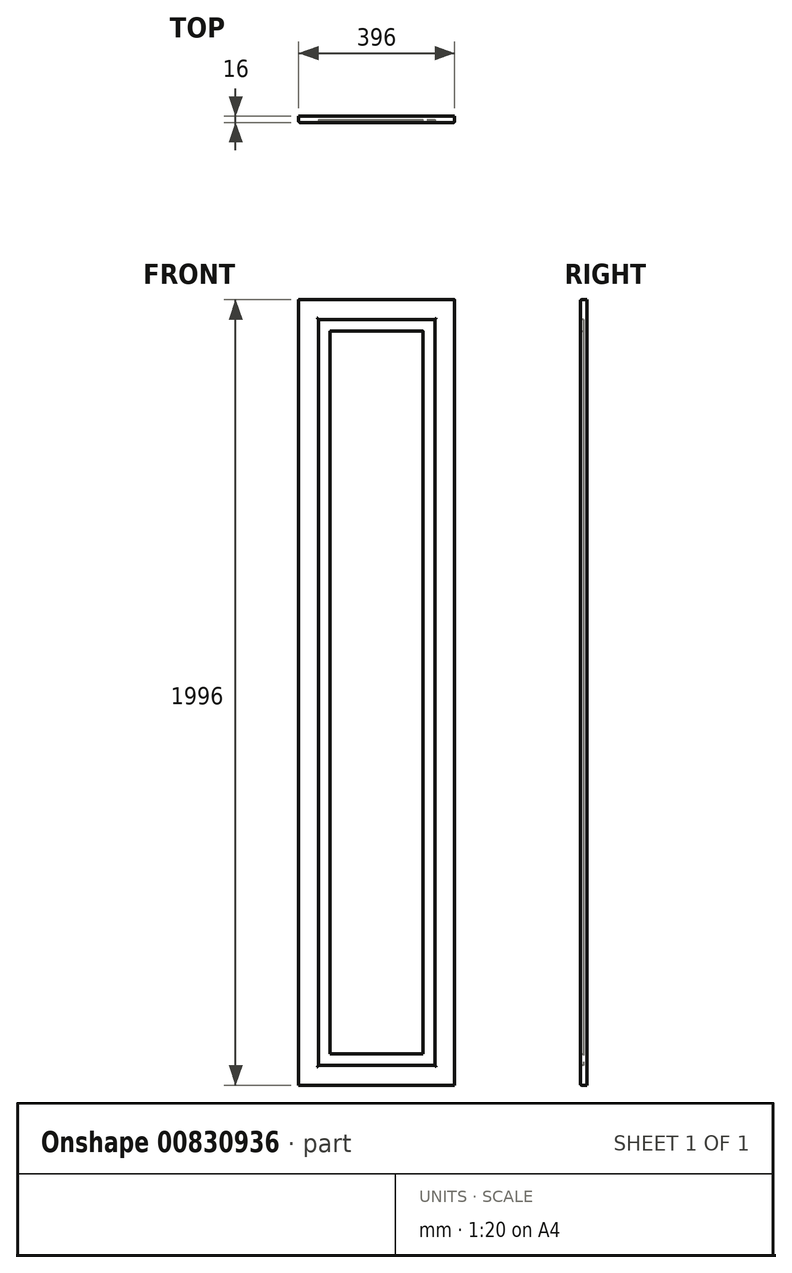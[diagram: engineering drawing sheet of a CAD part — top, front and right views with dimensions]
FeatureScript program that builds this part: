
annotation { "Feature Type Name" : "Feature", "Feature Type Description" : "" }
export const myFeature = defineFeature(function(context is Context, id is Id, definition is map)
    precondition{}
    {
        {
            var Q0;
            Q0=qCreatedBy(makeId("Front.planeOp"),FACE);
            var sketch = newSketch(context, id + "F0", { "sketchPlane" : qUnion([Q0])});
            skLineSegment(sketch, "E0.bottom", {"start": v(0, 0) * mm, "end": v(44.66, 0) * mm});
            skLineSegment(sketch, "E0.top", {"start": v(0, 33.8) * mm, "end": v(44.66, 33.8) * mm});
            skLineSegment(sketch, "E0.left", {"start": v(0, 0) * mm, "end": v(0, 33.8) * mm});
            skLineSegment(sketch, "E0.right", {"start": v(44.66, 0) * mm, "end": v(44.66, 33.8) * mm});
            skSolve(sketch);
        }
        {
            var Q0;
            Q0=makeQuery(id+"F0.imprint","IMPRINT",FACE,{"disambiguationData":[TD([[makeQuery(id+"F0.imprint","IMPRINT",EDGE,{"derivedFrom":sQuery(id+"F0.wireOp",EDGE,"E0.bottom")}),1.0]])]});
            extrude(context, id + "F1", {"entities" : qUnion([Q0]), "depth" : 16 * mm, "offsetDistance" : 25.4 * mm});
        }
        {
            var Q0;
            Q0=makeQuery(id+"F1.opExtrude","SWEPT_FACE",FACE,{"disambiguationData":[OSD([sQuery(id+"F0.wireOp",EDGE,"E0.bottom")])]});
            extrude(context, id + "F2", {"entities" : qUnion([Q0]), "operationType" : NewBodyOperationType.ADD, "oppositeDirection" : true, "depth" : 796 * mm, "offsetDistance" : 25 * mm});
        }
        {
            var Q0;
            {var subQ0=sQuery(id+"F0.wireOp",EDGE,"E0.left");Q0=makeQuery(id+"F2.boolean.opBoolean","MERGE",FACE,{"derivedFrom":[makeQuery(id+"F1.opExtrude","SWEPT_FACE",FACE,{"disambiguationData":[OSD([subQ0])]}),makeQuery(id+"F2.opExtrude","SWEPT_FACE",FACE,{"disambiguationData":[OSD([sQuery(id+"F0.wireOp",EDGE,"E0.bottom"),subQ0])]})]});}
            extrude(context, id + "F3", {"entities" : qUnion([Q0]), "operationType" : NewBodyOperationType.ADD, "oppositeDirection" : true, "depth" : 196 * mm, "offsetDistance" : 25 * mm});
        }
        {
            var Q0;
            {var subQ0=sQuery(id+"F0.wireOp",EDGE,"E0.left");var subQ1=sQuery(id+"F0.wireOp",EDGE,"E0.bottom");Q0=makeQuery(id+"F3.boolean.opBoolean","MERGE",FACE,{"derivedFrom":[makeQuery(id+"F2.boolean.opBoolean","MERGE",FACE,{"derivedFrom":[makeQuery(id+"F1.opExtrude","CAP_FACE",FACE,{"disambiguationData":[OSD([subQ1,sQuery(id+"F0.wireOp",EDGE,"E0.top"),subQ0,sQuery(id+"F0.wireOp",EDGE,"E0.right")])],"isStart":false}),makeQuery(id+"F2.opExtrude","SWEPT_FACE",FACE,{"disambiguationData":[OSD([subQ1]),TDD([makeQuery(id+"F1.opExtrude","CAP_EDGE",EDGE,{"disambiguationData":[OSD([subQ1])],"isStart":false})])]})]}),makeQuery(id+"F3.opExtrude","SWEPT_FACE",FACE,{"disambiguationData":[OSD([subQ1,subQ0]),TDD([makeQuery(id+"F2.boolean.opBoolean","MERGE",EDGE,{"derivedFrom":[makeQuery(id+"F1.opExtrude","CAP_EDGE",EDGE,{"disambiguationData":[OSD([subQ0])],"isStart":false}),makeQuery(id+"F2.opExtrude","SWEPT_EDGE",EDGE,{"disambiguationData":[OSD([subQ1,subQ0]),TDD([makeQuery(id+"F1.opExtrude","CAP_VERTEX",VERTEX,{"disambiguationData":[OSD([subQ1,subQ0])],"isStart":false})])]})]})])]})]});}
            var sketch = newSketch(context, id + "F4", { "sketchPlane" : qUnion([Q0])});
            skLineSegment(sketch, "E1.bottom", {"start": v(59.7, 646.67) * mm, "end": v(128.66, 646.67) * mm});
            skLineSegment(sketch, "E1.top", {"start": v(59.7, 152.97) * mm, "end": v(128.66, 152.97) * mm});
            skLineSegment(sketch, "E1.left", {"start": v(59.7, 646.67) * mm, "end": v(59.7, 152.97) * mm});
            skLineSegment(sketch, "E1.right", {"start": v(128.66, 646.67) * mm, "end": v(128.66, 152.97) * mm});
            skSolve(sketch);
        }
        {
            var Q0;
            Q0=makeQuery(id+"F4.imprint","IMPRINT",FACE,{"disambiguationData":[TD([[makeQuery(id+"F4.imprint","IMPRINT",EDGE,{"derivedFrom":sQuery(id+"F4.wireOp",EDGE,"E1.bottom")}),-1.0]])]});
            extrude(context, id + "F5", {"entities" : qUnion([Q0]), "operationType" : NewBodyOperationType.REMOVE, "oppositeDirection" : true, "depth" : 7 * mm, "offsetDistance" : 25 * mm});
        }
        {
            var Q0;
            Q0=makeQuery(id+"F5.boolean.opBoolean","COPY",FACE,{"derivedFrom":makeQuery(id+"F5.opExtrude","SWEPT_FACE",FACE,{"disambiguationData":[OSD([sQuery(id+"F4.wireOp",EDGE,"E1.left")])]})});
            extrude(context, id + "F6", {"entities" : qUnion([Q0]), "operationType" : NewBodyOperationType.REMOVE, "oppositeDirection" : true, "depth" : 9.7 * mm, "offsetDistance" : 25 * mm});
        }
        {
            var Q0;
            {var subQ0=sQuery(id+"F4.wireOp",EDGE,"E1.bottom");Q0=makeQuery(id+"F6.boolean.opBoolean","MERGE",FACE,{"derivedFrom":[makeQuery(id+"F5.boolean.opBoolean","COPY",FACE,{"derivedFrom":makeQuery(id+"F5.opExtrude","SWEPT_FACE",FACE,{"disambiguationData":[OSD([subQ0])]})}),makeQuery(id+"F6.opExtrude","SWEPT_FACE",FACE,{"disambiguationData":[OSD([subQ0,sQuery(id+"F4.wireOp",EDGE,"E1.left")])]})]});}
            extrude(context, id + "F7", {"entities" : qUnion([Q0]), "operationType" : NewBodyOperationType.ADD, "oppositeDirection" : true, "depth" : 99.33 * mm, "offsetDistance" : 25 * mm});
        }
        {
            var Q0;
            {var subQ0=sQuery(id+"F4.wireOp",EDGE,"E1.bottom");Q0=makeQuery(id+"F6.boolean.opBoolean","MERGE",FACE,{"derivedFrom":[makeQuery(id+"F5.boolean.opBoolean","COPY",FACE,{"derivedFrom":makeQuery(id+"F5.opExtrude","SWEPT_FACE",FACE,{"disambiguationData":[OSD([subQ0])]})}),makeQuery(id+"F6.opExtrude","SWEPT_FACE",FACE,{"disambiguationData":[OSD([subQ0,sQuery(id+"F4.wireOp",EDGE,"E1.left")])]})]});}
            extrude(context, id + "F8", {"entities" : qUnion([Q0]), "operationType" : NewBodyOperationType.REMOVE, "oppositeDirection" : true, "depth" : 99.33 * mm, "offsetDistance" : 25 * mm});
        }
        {
            var Q0;
            {var subQ0=sQuery(id+"F4.wireOp",EDGE,"E1.right");Q0=makeQuery(id+"F8.boolean.opBoolean","MERGE",FACE,{"derivedFrom":[makeQuery(id+"F5.boolean.opBoolean","COPY",FACE,{"derivedFrom":makeQuery(id+"F5.opExtrude","SWEPT_FACE",FACE,{"disambiguationData":[OSD([subQ0])]})}),makeQuery(id+"F8.opExtrude","SWEPT_FACE",FACE,{"disambiguationData":[OSD([sQuery(id+"F4.wireOp",EDGE,"E1.bottom"),subQ0])]})]});}
            extrude(context, id + "F9", {"entities" : qUnion([Q0]), "operationType" : NewBodyOperationType.REMOVE, "oppositeDirection" : true, "depth" : 17.34 * mm, "offsetDistance" : 25 * mm});
        }
        {
            var Q0;
            {var subQ0=sQuery(id+"F4.wireOp",EDGE,"E1.top");Q0=makeQuery(id+"F9.boolean.opBoolean","MERGE",FACE,{"derivedFrom":[makeQuery(id+"F6.boolean.opBoolean","MERGE",FACE,{"derivedFrom":[makeQuery(id+"F5.boolean.opBoolean","COPY",FACE,{"derivedFrom":makeQuery(id+"F5.opExtrude","SWEPT_FACE",FACE,{"disambiguationData":[OSD([subQ0])]})}),makeQuery(id+"F6.opExtrude","SWEPT_FACE",FACE,{"disambiguationData":[OSD([subQ0,sQuery(id+"F4.wireOp",EDGE,"E1.left")])]})]}),makeQuery(id+"F9.opExtrude","SWEPT_FACE",FACE,{"disambiguationData":[OSD([subQ0,sQuery(id+"F4.wireOp",EDGE,"E1.right")])]})]});}
            extrude(context, id + "F10", {"entities" : qUnion([Q0]), "operationType" : NewBodyOperationType.REMOVE, "oppositeDirection" : true, "depth" : 102.97 * mm, "offsetDistance" : 25 * mm});
        }
        {
            var Q0;
            {var subQ0=sQuery(id+"F4.wireOp",EDGE,"E1.right");var subQ1=sQuery(id+"F4.wireOp",EDGE,"E1.top");var subQ2=sQuery(id+"F4.wireOp",EDGE,"E1.left");var subQ3=sQuery(id+"F4.wireOp",EDGE,"E1.bottom");Q0=makeQuery(id+"F10.boolean.opBoolean","MERGE",FACE,{"derivedFrom":[makeQuery(id+"F9.boolean.opBoolean","MERGE",FACE,{"derivedFrom":[makeQuery(id+"F8.boolean.opBoolean","MERGE",FACE,{"derivedFrom":[makeQuery(id+"F6.boolean.opBoolean","MERGE",FACE,{"derivedFrom":[makeQuery(id+"F5.boolean.opBoolean","COPY",FACE,{"derivedFrom":makeQuery(id+"F5.opExtrude","CAP_FACE",FACE,{"disambiguationData":[OSD([subQ3,subQ1,subQ2,subQ0])],"isStart":false})}),makeQuery(id+"F6.opExtrude","SWEPT_FACE",FACE,{"disambiguationData":[OSD([subQ2]),TDD([makeQuery(id+"F5.boolean.opBoolean","COPY",EDGE,{"derivedFrom":makeQuery(id+"F5.opExtrude","CAP_EDGE",EDGE,{"disambiguationData":[OSD([subQ2])],"isStart":false})})])]})]}),makeQuery(id+"F8.opExtrude","SWEPT_FACE",FACE,{"disambiguationData":[OSD([subQ3,subQ2]),TDD([makeQuery(id+"F6.boolean.opBoolean","MERGE",EDGE,{"derivedFrom":[makeQuery(id+"F5.boolean.opBoolean","COPY",EDGE,{"derivedFrom":makeQuery(id+"F5.opExtrude","CAP_EDGE",EDGE,{"disambiguationData":[OSD([subQ3])],"isStart":false})}),makeQuery(id+"F6.opExtrude","SWEPT_EDGE",EDGE,{"disambiguationData":[OSD([subQ3,subQ2]),TDD([makeQuery(id+"F5.boolean.opBoolean","COPY",VERTEX,{"derivedFrom":makeQuery(id+"F5.opExtrude","CAP_VERTEX",VERTEX,{"disambiguationData":[OSD([subQ3,subQ2])],"isStart":false})})])]})]})])]})]}),makeQuery(id+"F9.opExtrude","SWEPT_FACE",FACE,{"disambiguationData":[OSD([subQ3,subQ0]),TDD([makeQuery(id+"F8.boolean.opBoolean","MERGE",EDGE,{"derivedFrom":[makeQuery(id+"F5.boolean.opBoolean","COPY",EDGE,{"derivedFrom":makeQuery(id+"F5.opExtrude","CAP_EDGE",EDGE,{"disambiguationData":[OSD([subQ0])],"isStart":false})}),makeQuery(id+"F8.opExtrude","SWEPT_EDGE",EDGE,{"disambiguationData":[OSD([subQ3,subQ0]),TDD([makeQuery(id+"F5.boolean.opBoolean","COPY",VERTEX,{"derivedFrom":makeQuery(id+"F5.opExtrude","CAP_VERTEX",VERTEX,{"disambiguationData":[OSD([subQ3,subQ0])],"isStart":false})})])]})]})])]})]}),makeQuery(id+"F10.opExtrude","SWEPT_FACE",FACE,{"disambiguationData":[OSD([subQ1,subQ2,subQ0]),TDD([makeQuery(id+"F9.boolean.opBoolean","MERGE",EDGE,{"derivedFrom":[makeQuery(id+"F6.boolean.opBoolean","MERGE",EDGE,{"derivedFrom":[makeQuery(id+"F5.boolean.opBoolean","COPY",EDGE,{"derivedFrom":makeQuery(id+"F5.opExtrude","CAP_EDGE",EDGE,{"disambiguationData":[OSD([subQ1])],"isStart":false})}),makeQuery(id+"F6.opExtrude","SWEPT_EDGE",EDGE,{"disambiguationData":[OSD([subQ1,subQ2]),TDD([makeQuery(id+"F5.boolean.opBoolean","COPY",VERTEX,{"derivedFrom":makeQuery(id+"F5.opExtrude","CAP_VERTEX",VERTEX,{"disambiguationData":[OSD([subQ1,subQ2])],"isStart":false})})])]})]}),makeQuery(id+"F9.opExtrude","SWEPT_EDGE",EDGE,{"disambiguationData":[OSD([subQ1,subQ0]),TDD([makeQuery(id+"F5.boolean.opBoolean","COPY",VERTEX,{"derivedFrom":makeQuery(id+"F5.opExtrude","CAP_VERTEX",VERTEX,{"disambiguationData":[OSD([subQ1,subQ0])],"isStart":false})})])]})]})])]})]});}
            var sketch = newSketch(context, id + "F11", { "sketchPlane" : qUnion([Q0])});
            skLineSegment(sketch, "E2.bottom", {"start": v(74.13, 678.73) * mm, "end": v(109.41, 678.73) * mm});
            skLineSegment(sketch, "E2.top", {"start": v(74.13, 186.63) * mm, "end": v(109.41, 186.63) * mm});
            skLineSegment(sketch, "E2.left", {"start": v(74.13, 678.73) * mm, "end": v(74.13, 186.63) * mm});
            skLineSegment(sketch, "E2.right", {"start": v(109.41, 678.73) * mm, "end": v(109.41, 186.63) * mm});
            skSolve(sketch);
        }
        {
            var Q0;
            Q0=makeQuery(id+"F11.imprint","IMPRINT",FACE,{"disambiguationData":[TD([[makeQuery(id+"F11.imprint","IMPRINT",EDGE,{"derivedFrom":sQuery(id+"F11.wireOp",EDGE,"E2.bottom")}),-1.0]])]});
            extrude(context, id + "F12", {"entities" : qUnion([Q0]), "operationType" : NewBodyOperationType.ADD, "depth" : 7 * mm, "offsetDistance" : 25 * mm});
        }
        {
            var Q0;
            Q0=makeQuery(id+"F12.opExtrude","SWEPT_FACE",FACE,{"disambiguationData":[OSD([sQuery(id+"F11.wireOp",EDGE,"E2.bottom")])]});
            extrude(context, id + "F13", {"entities" : qUnion([Q0]), "operationType" : NewBodyOperationType.ADD, "depth" : 37.27 * mm, "offsetDistance" : 25 * mm});
        }
        {
            var Q0;
            {var subQ0=sQuery(id+"F11.wireOp",EDGE,"E2.right");Q0=makeQuery(id+"F13.boolean.opBoolean","MERGE",FACE,{"derivedFrom":[makeQuery(id+"F12.opExtrude","SWEPT_FACE",FACE,{"disambiguationData":[OSD([subQ0])]}),makeQuery(id+"F13.opExtrude","SWEPT_FACE",FACE,{"disambiguationData":[OSD([sQuery(id+"F11.wireOp",EDGE,"E2.bottom"),subQ0])]})]});}
            extrude(context, id + "F14", {"entities" : qUnion([Q0]), "operationType" : NewBodyOperationType.ADD, "depth" : 6.58 * mm, "offsetDistance" : 25 * mm});
        }
        {
            var Q0;
            {var subQ0=sQuery(id+"F11.wireOp",EDGE,"E2.top");Q0=makeQuery(id+"F14.boolean.opBoolean","MERGE",FACE,{"derivedFrom":[makeQuery(id+"F12.opExtrude","SWEPT_FACE",FACE,{"disambiguationData":[OSD([subQ0])]}),makeQuery(id+"F14.opExtrude","SWEPT_FACE",FACE,{"disambiguationData":[OSD([subQ0,sQuery(id+"F11.wireOp",EDGE,"E2.right")])]})]});}
            extrude(context, id + "F15", {"entities" : qUnion([Q0]), "operationType" : NewBodyOperationType.ADD, "depth" : 106.63 * mm, "offsetDistance" : 25 * mm});
        }
        {
            var Q0;
            {var subQ0=sQuery(id+"F11.wireOp",EDGE,"E2.left");Q0=makeQuery(id+"F15.boolean.opBoolean","MERGE",FACE,{"derivedFrom":[makeQuery(id+"F13.boolean.opBoolean","MERGE",FACE,{"derivedFrom":[makeQuery(id+"F12.opExtrude","SWEPT_FACE",FACE,{"disambiguationData":[OSD([subQ0])]}),makeQuery(id+"F13.opExtrude","SWEPT_FACE",FACE,{"disambiguationData":[OSD([sQuery(id+"F11.wireOp",EDGE,"E2.bottom"),subQ0])]})]}),makeQuery(id+"F15.opExtrude","SWEPT_FACE",FACE,{"disambiguationData":[OSD([sQuery(id+"F11.wireOp",EDGE,"E2.top"),subQ0])]})]});}
            extrude(context, id + "F16", {"entities" : qUnion([Q0]), "operationType" : NewBodyOperationType.REMOVE, "oppositeDirection" : true, "depth" : 5.87 * mm, "offsetDistance" : 25 * mm});
        }
        {
            var Q0;
            Q0=makeQuery(id+"F3.opExtrude","CAP_FACE",FACE,{"disambiguationData":[OSD([sQuery(id+"F0.wireOp",EDGE,"E0.bottom"),sQuery(id+"F0.wireOp",EDGE,"E0.left")])],"isStart":false});
            extrude(context, id + "F17", {"entities" : qUnion([Q0]), "operationType" : NewBodyOperationType.ADD, "depth" : 200 * mm, "offsetDistance" : 25 * mm});
        }
        {
            var Q0;
            {var subQ0=sQuery(id+"F4.wireOp",EDGE,"E1.right");Q0=makeQuery(id+"F10.boolean.opBoolean","MERGE",FACE,{"derivedFrom":[makeQuery(id+"F9.boolean.opBoolean","COPY",FACE,{"derivedFrom":makeQuery(id+"F9.opExtrude","CAP_FACE",FACE,{"disambiguationData":[OSD([sQuery(id+"F4.wireOp",EDGE,"E1.bottom"),subQ0])],"isStart":false})}),makeQuery(id+"F10.opExtrude","SWEPT_FACE",FACE,{"disambiguationData":[OSD([sQuery(id+"F4.wireOp",EDGE,"E1.top"),subQ0])]})]});}
            extrude(context, id + "F18", {"entities" : qUnion([Q0]), "operationType" : NewBodyOperationType.REMOVE, "oppositeDirection" : true, "depth" : 200 * mm, "offsetDistance" : 25 * mm});
        }
        {
            var Q0;
            {var subQ0=sQuery(id+"F11.wireOp",EDGE,"E2.right");var subQ1=sQuery(id+"F11.wireOp",EDGE,"E2.top");Q0=makeQuery(id+"F15.boolean.opBoolean","MERGE",FACE,{"derivedFrom":[makeQuery(id+"F14.opExtrude","CAP_FACE",FACE,{"disambiguationData":[OSD([sQuery(id+"F11.wireOp",EDGE,"E2.bottom"),subQ0])],"isStart":false}),makeQuery(id+"F15.opExtrude","SWEPT_FACE",FACE,{"disambiguationData":[OSD([subQ1,subQ0]),TDD([makeQuery(id+"F14.opExtrude","CAP_EDGE",EDGE,{"disambiguationData":[OSD([subQ1,subQ0])],"isStart":false})])]})]});}
            extrude(context, id + "F19", {"entities" : qUnion([Q0]), "operationType" : NewBodyOperationType.ADD, "depth" : 200 * mm, "offsetDistance" : 25 * mm});
        }
        {
            var Q0;
            Q0=makeQuery(id+"F17.opExtrude","CAP_FACE",FACE,{"disambiguationData":[OSD([sQuery(id+"F0.wireOp",EDGE,"E0.bottom"),sQuery(id+"F0.wireOp",EDGE,"E0.left")])],"isStart":false});
            extrude(context, id + "F20", {"entities" : qUnion([Q0]), "operationType" : NewBodyOperationType.ADD, "depth" : 200 * mm, "offsetDistance" : 25 * mm});
        }
        {
            var Q0;
            Q0=makeQuery(id+"F18.boolean.opBoolean","COPY",FACE,{"derivedFrom":makeQuery(id+"F18.opExtrude","CAP_FACE",FACE,{"disambiguationData":[OSD([sQuery(id+"F4.wireOp",EDGE,"E1.bottom"),sQuery(id+"F4.wireOp",EDGE,"E1.top"),sQuery(id+"F4.wireOp",EDGE,"E1.right")])],"isStart":false})});
            extrude(context, id + "F21", {"entities" : qUnion([Q0]), "operationType" : NewBodyOperationType.REMOVE, "oppositeDirection" : true, "depth" : 200 * mm, "offsetDistance" : 25 * mm});
        }
        {
            var Q0;
            Q0=makeQuery(id+"F19.opExtrude","CAP_FACE",FACE,{"disambiguationData":[OSD([sQuery(id+"F11.wireOp",EDGE,"E2.bottom"),sQuery(id+"F11.wireOp",EDGE,"E2.top"),sQuery(id+"F11.wireOp",EDGE,"E2.right")])],"isStart":false});
            extrude(context, id + "F22", {"entities" : qUnion([Q0]), "operationType" : NewBodyOperationType.ADD, "depth" : 200 * mm, "offsetDistance" : 25 * mm});
        }
        {
            var Q0;
            Q0=makeQuery(id+"F20.opExtrude","CAP_FACE",FACE,{"disambiguationData":[OSD([sQuery(id+"F0.wireOp",EDGE,"E0.bottom"),sQuery(id+"F0.wireOp",EDGE,"E0.left")])],"isStart":false});
            extrude(context, id + "F23", {"entities" : qUnion([Q0]), "operationType" : NewBodyOperationType.ADD, "depth" : 400 * mm, "offsetDistance" : 25 * mm});
        }
        {
            var Q0;
            Q0=makeQuery(id+"F21.boolean.opBoolean","COPY",FACE,{"derivedFrom":makeQuery(id+"F21.opExtrude","CAP_FACE",FACE,{"disambiguationData":[OSD([sQuery(id+"F4.wireOp",EDGE,"E1.bottom"),sQuery(id+"F4.wireOp",EDGE,"E1.top"),sQuery(id+"F4.wireOp",EDGE,"E1.right")])],"isStart":false})});
            extrude(context, id + "F24", {"entities" : qUnion([Q0]), "operationType" : NewBodyOperationType.REMOVE, "oppositeDirection" : true, "depth" : 400 * mm, "offsetDistance" : 25 * mm});
        }
        {
            var Q0;
            Q0=makeQuery(id+"F22.opExtrude","CAP_FACE",FACE,{"disambiguationData":[OSD([sQuery(id+"F11.wireOp",EDGE,"E2.bottom"),sQuery(id+"F11.wireOp",EDGE,"E2.top"),sQuery(id+"F11.wireOp",EDGE,"E2.right")])],"isStart":false});
            extrude(context, id + "F25", {"entities" : qUnion([Q0]), "operationType" : NewBodyOperationType.ADD, "depth" : 400 * mm, "offsetDistance" : 25 * mm});
        }
        {
            var Q0;
            {var subQ0=sQuery(id+"F11.wireOp",EDGE,"E2.right");var subQ1=sQuery(id+"F11.wireOp",EDGE,"E2.top");Q0=makeQuery(id+"F25.boolean.opBoolean","MERGE",FACE,{"derivedFrom":[makeQuery(id+"F22.boolean.opBoolean","MERGE",FACE,{"derivedFrom":[makeQuery(id+"F19.boolean.opBoolean","MERGE",FACE,{"derivedFrom":[makeQuery(id+"F15.opExtrude","CAP_FACE",FACE,{"disambiguationData":[OSD([subQ1,subQ0])],"isStart":false}),makeQuery(id+"F19.opExtrude","SWEPT_FACE",FACE,{"disambiguationData":[OSD([subQ1,subQ0])]})]}),makeQuery(id+"F22.opExtrude","SWEPT_FACE",FACE,{"disambiguationData":[OSD([subQ1,subQ0])]})]}),makeQuery(id+"F25.opExtrude","SWEPT_FACE",FACE,{"disambiguationData":[OSD([subQ1,subQ0])]})]});}
            extrude(context, id + "F26", {"entities" : qUnion([Q0]), "operationType" : NewBodyOperationType.REMOVE, "oppositeDirection" : true, "depth" : 400 * mm, "offsetDistance" : 25 * mm});
        }
        {
            var Q0;
            {var subQ0=sQuery(id+"F4.wireOp",EDGE,"E1.right");var subQ1=sQuery(id+"F4.wireOp",EDGE,"E1.top");Q0=makeQuery(id+"F24.boolean.opBoolean","MERGE",FACE,{"derivedFrom":[makeQuery(id+"F21.boolean.opBoolean","MERGE",FACE,{"derivedFrom":[makeQuery(id+"F18.boolean.opBoolean","MERGE",FACE,{"derivedFrom":[makeQuery(id+"F10.boolean.opBoolean","COPY",FACE,{"derivedFrom":makeQuery(id+"F10.opExtrude","CAP_FACE",FACE,{"disambiguationData":[OSD([subQ1,sQuery(id+"F4.wireOp",EDGE,"E1.left"),subQ0])],"isStart":false})}),makeQuery(id+"F18.opExtrude","SWEPT_FACE",FACE,{"disambiguationData":[OSD([subQ1,subQ0])]})]}),makeQuery(id+"F21.opExtrude","SWEPT_FACE",FACE,{"disambiguationData":[OSD([subQ1,subQ0])]})]}),makeQuery(id+"F24.opExtrude","SWEPT_FACE",FACE,{"disambiguationData":[OSD([subQ1,subQ0])]})]});}
            extrude(context, id + "F27", {"entities" : qUnion([Q0]), "operationType" : NewBodyOperationType.ADD, "depth" : 400 * mm, "offsetDistance" : 25 * mm});
        }
        {
            var Q0;
            {var subQ0=sQuery(id+"F0.wireOp",EDGE,"E0.left");var subQ1=sQuery(id+"F0.wireOp",EDGE,"E0.bottom");var subQ2=makeQuery(id+"F1.opExtrude","SWEPT_EDGE",EDGE,{"disambiguationData":[OSD([subQ1,subQ0])]});var subQ3=makeQuery(id+"F3.opExtrude","CAP_EDGE",EDGE,{"disambiguationData":[OSD([subQ1,subQ0]),TDD([subQ2])],"isStart":false});var subQ4=makeQuery(id+"F17.opExtrude","CAP_EDGE",EDGE,{"disambiguationData":[OSD([subQ1,subQ0]),TDD([subQ3])],"isStart":false});Q0=makeQuery(id+"F23.boolean.opBoolean","MERGE",FACE,{"derivedFrom":[makeQuery(id+"F20.boolean.opBoolean","MERGE",FACE,{"derivedFrom":[makeQuery(id+"F17.boolean.opBoolean","MERGE",FACE,{"derivedFrom":[makeQuery(id+"F3.boolean.opBoolean","MERGE",FACE,{"derivedFrom":[makeQuery(id+"F1.opExtrude","SWEPT_FACE",FACE,{"disambiguationData":[OSD([subQ1])]}),makeQuery(id+"F3.opExtrude","SWEPT_FACE",FACE,{"disambiguationData":[OSD([subQ1,subQ0]),TDD([subQ2])]})]}),makeQuery(id+"F17.opExtrude","SWEPT_FACE",FACE,{"disambiguationData":[OSD([subQ1,subQ0]),TDD([subQ3])]})]}),makeQuery(id+"F20.opExtrude","SWEPT_FACE",FACE,{"disambiguationData":[OSD([subQ1,subQ0]),TDD([subQ4])]})]}),makeQuery(id+"F23.opExtrude","SWEPT_FACE",FACE,{"disambiguationData":[OSD([subQ1,subQ0]),TDD([makeQuery(id+"F20.opExtrude","CAP_EDGE",EDGE,{"disambiguationData":[OSD([subQ1,subQ0]),TDD([subQ4])],"isStart":false})])]})]});}
            extrude(context, id + "F28", {"entities" : qUnion([Q0]), "operationType" : NewBodyOperationType.REMOVE, "oppositeDirection" : true, "depth" : 400 * mm, "offsetDistance" : 25 * mm});
        }
        {
            var Q0;
            Q0=makeQuery(id+"F23.opExtrude","CAP_FACE",FACE,{"disambiguationData":[OSD([sQuery(id+"F0.wireOp",EDGE,"E0.bottom"),sQuery(id+"F0.wireOp",EDGE,"E0.left")])],"isStart":false});
            extrude(context, id + "F29", {"entities" : qUnion([Q0]), "operationType" : NewBodyOperationType.ADD, "depth" : 400 * mm, "offsetDistance" : 25 * mm});
        }
        {
            var Q0;
            Q0=makeQuery(id+"F24.boolean.opBoolean","COPY",FACE,{"derivedFrom":makeQuery(id+"F24.opExtrude","CAP_FACE",FACE,{"disambiguationData":[OSD([sQuery(id+"F4.wireOp",EDGE,"E1.bottom"),sQuery(id+"F4.wireOp",EDGE,"E1.top"),sQuery(id+"F4.wireOp",EDGE,"E1.right")])],"isStart":false})});
            extrude(context, id + "F30", {"entities" : qUnion([Q0]), "operationType" : NewBodyOperationType.REMOVE, "oppositeDirection" : true, "depth" : 400 * mm, "offsetDistance" : 25 * mm});
        }
        {
            var Q0;
            Q0=makeQuery(id+"F25.opExtrude","CAP_FACE",FACE,{"disambiguationData":[OSD([sQuery(id+"F11.wireOp",EDGE,"E2.bottom"),sQuery(id+"F11.wireOp",EDGE,"E2.top"),sQuery(id+"F11.wireOp",EDGE,"E2.right")])],"isStart":false});
            extrude(context, id + "F31", {"entities" : qUnion([Q0]), "operationType" : NewBodyOperationType.ADD, "depth" : 400 * mm, "offsetDistance" : 25 * mm});
        }
        {
            var Q0;
            Q0=makeQuery(id+"F31.opExtrude","CAP_FACE",FACE,{"disambiguationData":[OSD([sQuery(id+"F11.wireOp",EDGE,"E2.bottom"),sQuery(id+"F11.wireOp",EDGE,"E2.top"),sQuery(id+"F11.wireOp",EDGE,"E2.right")])],"isStart":false});
            extrude(context, id + "F32", {"entities" : qUnion([Q0]), "operationType" : NewBodyOperationType.REMOVE, "oppositeDirection" : true, "depth" : 1000 * mm, "offsetDistance" : 25 * mm});
        }
        {
            var Q0;
            Q0=makeQuery(id+"F30.boolean.opBoolean","COPY",FACE,{"derivedFrom":makeQuery(id+"F30.opExtrude","CAP_FACE",FACE,{"disambiguationData":[OSD([sQuery(id+"F4.wireOp",EDGE,"E1.bottom"),sQuery(id+"F4.wireOp",EDGE,"E1.top"),sQuery(id+"F4.wireOp",EDGE,"E1.right")])],"isStart":false})});
            extrude(context, id + "F33", {"entities" : qUnion([Q0]), "operationType" : NewBodyOperationType.ADD, "depth" : 1000 * mm, "offsetDistance" : 25 * mm});
        }
        {
            var Q0;
            Q0=makeQuery(id+"F29.opExtrude","CAP_FACE",FACE,{"disambiguationData":[OSD([sQuery(id+"F0.wireOp",EDGE,"E0.bottom"),sQuery(id+"F0.wireOp",EDGE,"E0.left")])],"isStart":false});
            extrude(context, id + "F34", {"entities" : qUnion([Q0]), "operationType" : NewBodyOperationType.REMOVE, "oppositeDirection" : true, "depth" : 1000 * mm, "offsetDistance" : 25 * mm});
        }
        {
            var Q0;
            {var subQ0=sQuery(id+"F0.wireOp",EDGE,"E0.left");var subQ1=sQuery(id+"F0.wireOp",EDGE,"E0.bottom");var subQ2=makeQuery(id+"F2.opExtrude","CAP_EDGE",EDGE,{"disambiguationData":[OSD([subQ1,subQ0])],"isStart":false});var subQ3=makeQuery(id+"F3.opExtrude","CAP_EDGE",EDGE,{"disambiguationData":[OSD([subQ1,subQ0]),TDD([subQ2])],"isStart":false});var subQ4=makeQuery(id+"F17.opExtrude","CAP_EDGE",EDGE,{"disambiguationData":[OSD([subQ1,subQ0]),TDD([subQ3])],"isStart":false});var subQ5=makeQuery(id+"F20.opExtrude","CAP_EDGE",EDGE,{"disambiguationData":[OSD([subQ1,subQ0]),TDD([subQ4])],"isStart":false});Q0=makeQuery(id+"F29.boolean.opBoolean","MERGE",FACE,{"derivedFrom":[makeQuery(id+"F23.boolean.opBoolean","MERGE",FACE,{"derivedFrom":[makeQuery(id+"F20.boolean.opBoolean","MERGE",FACE,{"derivedFrom":[makeQuery(id+"F17.boolean.opBoolean","MERGE",FACE,{"derivedFrom":[makeQuery(id+"F3.boolean.opBoolean","MERGE",FACE,{"derivedFrom":[makeQuery(id+"F2.opExtrude","CAP_FACE",FACE,{"disambiguationData":[OSD([subQ1])],"isStart":false}),makeQuery(id+"F3.opExtrude","SWEPT_FACE",FACE,{"disambiguationData":[OSD([subQ1,subQ0]),TDD([subQ2])]})]}),makeQuery(id+"F17.opExtrude","SWEPT_FACE",FACE,{"disambiguationData":[OSD([subQ1,subQ0]),TDD([subQ3])]})]}),makeQuery(id+"F20.opExtrude","SWEPT_FACE",FACE,{"disambiguationData":[OSD([subQ1,subQ0]),TDD([subQ4])]})]}),makeQuery(id+"F23.opExtrude","SWEPT_FACE",FACE,{"disambiguationData":[OSD([subQ1,subQ0]),TDD([subQ5])]})]}),makeQuery(id+"F29.opExtrude","SWEPT_FACE",FACE,{"disambiguationData":[OSD([subQ1,subQ0]),TDD([makeQuery(id+"F23.opExtrude","CAP_EDGE",EDGE,{"disambiguationData":[OSD([subQ1,subQ0]),TDD([subQ5])],"isStart":false})])]})]});}
            extrude(context, id + "F35", {"entities" : qUnion([Q0]), "operationType" : NewBodyOperationType.ADD, "depth" : 1000 * mm, "offsetDistance" : 25 * mm});
        }
        {
            var Q0;
            {var subQ0=sQuery(id+"F4.wireOp",EDGE,"E1.right");var subQ1=sQuery(id+"F4.wireOp",EDGE,"E1.bottom");Q0=makeQuery(id+"F30.boolean.opBoolean","MERGE",FACE,{"derivedFrom":[makeQuery(id+"F24.boolean.opBoolean","MERGE",FACE,{"derivedFrom":[makeQuery(id+"F21.boolean.opBoolean","MERGE",FACE,{"derivedFrom":[makeQuery(id+"F18.boolean.opBoolean","MERGE",FACE,{"derivedFrom":[makeQuery(id+"F9.boolean.opBoolean","MERGE",FACE,{"derivedFrom":[makeQuery(id+"F8.boolean.opBoolean","COPY",FACE,{"derivedFrom":makeQuery(id+"F8.opExtrude","CAP_FACE",FACE,{"disambiguationData":[OSD([subQ1,sQuery(id+"F4.wireOp",EDGE,"E1.left")])],"isStart":false})}),makeQuery(id+"F9.opExtrude","SWEPT_FACE",FACE,{"disambiguationData":[OSD([subQ1,subQ0]),TDD([makeQuery(id+"F8.boolean.opBoolean","COPY",EDGE,{"derivedFrom":makeQuery(id+"F8.opExtrude","CAP_EDGE",EDGE,{"disambiguationData":[OSD([subQ1,subQ0])],"isStart":false})})])]})]}),makeQuery(id+"F18.opExtrude","SWEPT_FACE",FACE,{"disambiguationData":[OSD([subQ1,subQ0])]})]}),makeQuery(id+"F21.opExtrude","SWEPT_FACE",FACE,{"disambiguationData":[OSD([subQ1,subQ0])]})]}),makeQuery(id+"F24.opExtrude","SWEPT_FACE",FACE,{"disambiguationData":[OSD([subQ1,subQ0])]})]}),makeQuery(id+"F30.opExtrude","SWEPT_FACE",FACE,{"disambiguationData":[OSD([subQ1,subQ0])]})]});}
            extrude(context, id + "F36", {"entities" : qUnion([Q0]), "operationType" : NewBodyOperationType.REMOVE, "oppositeDirection" : true, "depth" : 1000 * mm, "offsetDistance" : 25 * mm});
        }
        {
            var Q0;
            {var subQ0=sQuery(id+"F11.wireOp",EDGE,"E2.right");var subQ1=sQuery(id+"F11.wireOp",EDGE,"E2.bottom");Q0=makeQuery(id+"F31.boolean.opBoolean","MERGE",FACE,{"derivedFrom":[makeQuery(id+"F25.boolean.opBoolean","MERGE",FACE,{"derivedFrom":[makeQuery(id+"F22.boolean.opBoolean","MERGE",FACE,{"derivedFrom":[makeQuery(id+"F19.boolean.opBoolean","MERGE",FACE,{"derivedFrom":[makeQuery(id+"F14.boolean.opBoolean","MERGE",FACE,{"derivedFrom":[makeQuery(id+"F13.opExtrude","CAP_FACE",FACE,{"disambiguationData":[OSD([subQ1])],"isStart":false}),makeQuery(id+"F14.opExtrude","SWEPT_FACE",FACE,{"disambiguationData":[OSD([subQ1,subQ0]),TDD([makeQuery(id+"F13.opExtrude","CAP_EDGE",EDGE,{"disambiguationData":[OSD([subQ1,subQ0])],"isStart":false})])]})]}),makeQuery(id+"F19.opExtrude","SWEPT_FACE",FACE,{"disambiguationData":[OSD([subQ1,subQ0])]})]}),makeQuery(id+"F22.opExtrude","SWEPT_FACE",FACE,{"disambiguationData":[OSD([subQ1,subQ0])]})]}),makeQuery(id+"F25.opExtrude","SWEPT_FACE",FACE,{"disambiguationData":[OSD([subQ1,subQ0])]})]}),makeQuery(id+"F31.opExtrude","SWEPT_FACE",FACE,{"disambiguationData":[OSD([subQ1,subQ0])]})]});}
            extrude(context, id + "F37", {"entities" : qUnion([Q0]), "operationType" : NewBodyOperationType.ADD, "depth" : 1000 * mm, "offsetDistance" : 25 * mm});
        }
        {
            var Q0;
            Q0=makeQuery(id+"F35.opExtrude","CAP_FACE",FACE,{"disambiguationData":[OSD([sQuery(id+"F0.wireOp",EDGE,"E0.bottom"),sQuery(id+"F0.wireOp",EDGE,"E0.left")])],"isStart":false});
            extrude(context, id + "F38", {"entities" : qUnion([Q0]), "operationType" : NewBodyOperationType.ADD, "depth" : 600 * mm, "offsetDistance" : 25 * mm});
        }
        {
            var Q0;
            Q0=makeQuery(id+"F36.boolean.opBoolean","COPY",FACE,{"derivedFrom":makeQuery(id+"F36.opExtrude","CAP_FACE",FACE,{"disambiguationData":[OSD([sQuery(id+"F4.wireOp",EDGE,"E1.bottom"),sQuery(id+"F4.wireOp",EDGE,"E1.left"),sQuery(id+"F4.wireOp",EDGE,"E1.right")])],"isStart":false})});
            extrude(context, id + "F39", {"entities" : qUnion([Q0]), "operationType" : NewBodyOperationType.REMOVE, "oppositeDirection" : true, "depth" : 600 * mm, "offsetDistance" : 25 * mm});
        }
        {
            var Q0;
            Q0=makeQuery(id+"F37.opExtrude","CAP_FACE",FACE,{"disambiguationData":[OSD([sQuery(id+"F11.wireOp",EDGE,"E2.bottom"),sQuery(id+"F11.wireOp",EDGE,"E2.right")])],"isStart":false});
            extrude(context, id + "F40", {"entities" : qUnion([Q0]), "operationType" : NewBodyOperationType.ADD, "depth" : 600 * mm, "offsetDistance" : 25 * mm});
        }
        {
            var Q0;
            {var subQ0=sQuery(id+"F11.wireOp",EDGE,"E2.right");var subQ1=sQuery(id+"F11.wireOp",EDGE,"E2.bottom");var subQ2=makeQuery(id+"F12.opExtrude","CAP_VERTEX",VERTEX,{"disambiguationData":[OSD([subQ1,subQ0])],"isStart":false});var subQ3=makeQuery(id+"F13.opExtrude","CAP_VERTEX",VERTEX,{"disambiguationData":[OSD([subQ1,subQ0]),TDD([subQ2])],"isStart":false});var subQ4=makeQuery(id+"F14.opExtrude","CAP_VERTEX",VERTEX,{"disambiguationData":[OSD([subQ1,subQ0]),TDD([subQ3])],"isStart":false});var subQ5=makeQuery(id+"F19.opExtrude","CAP_VERTEX",VERTEX,{"disambiguationData":[OSD([subQ1,subQ0]),TDD([subQ4])],"isStart":false});var subQ6=makeQuery(id+"F22.opExtrude","CAP_VERTEX",VERTEX,{"disambiguationData":[OSD([subQ1,subQ0]),TDD([subQ5])],"isStart":false});var subQ7=makeQuery(id+"F12.opExtrude","CAP_EDGE",EDGE,{"disambiguationData":[OSD([subQ1])],"isStart":false});var subQ8=makeQuery(id+"F31.boolean.opBoolean","MERGE",EDGE,{"derivedFrom":[makeQuery(id+"F25.boolean.opBoolean","MERGE",EDGE,{"derivedFrom":[makeQuery(id+"F22.boolean.opBoolean","MERGE",EDGE,{"derivedFrom":[makeQuery(id+"F19.boolean.opBoolean","MERGE",EDGE,{"derivedFrom":[makeQuery(id+"F14.boolean.opBoolean","MERGE",EDGE,{"derivedFrom":[makeQuery(id+"F13.opExtrude","CAP_EDGE",EDGE,{"disambiguationData":[OSD([subQ1]),TDD([subQ7])],"isStart":false}),makeQuery(id+"F14.opExtrude","SWEPT_EDGE",EDGE,{"disambiguationData":[OSD([subQ1,subQ0]),TDD([subQ3])]})]}),makeQuery(id+"F19.opExtrude","SWEPT_EDGE",EDGE,{"disambiguationData":[OSD([subQ1,subQ0]),TDD([subQ4])]})]}),makeQuery(id+"F22.opExtrude","SWEPT_EDGE",EDGE,{"disambiguationData":[OSD([subQ1,subQ0]),TDD([subQ5])]})]}),makeQuery(id+"F25.opExtrude","SWEPT_EDGE",EDGE,{"disambiguationData":[OSD([subQ1,subQ0]),TDD([subQ6])]})]}),makeQuery(id+"F31.opExtrude","SWEPT_EDGE",EDGE,{"disambiguationData":[OSD([subQ1,subQ0]),TDD([makeQuery(id+"F25.opExtrude","CAP_VERTEX",VERTEX,{"disambiguationData":[OSD([subQ1,subQ0]),TDD([subQ6])],"isStart":false})])]})]});var subQ9=sQuery(id+"F11.wireOp",EDGE,"E2.top");var subQ10=makeQuery(id+"F12.opExtrude","CAP_VERTEX",VERTEX,{"disambiguationData":[OSD([subQ9,subQ0])],"isStart":false});var subQ11=makeQuery(id+"F13.boolean.opBoolean","MERGE",EDGE,{"derivedFrom":[makeQuery(id+"F12.opExtrude","CAP_EDGE",EDGE,{"disambiguationData":[OSD([subQ0])],"isStart":false}),makeQuery(id+"F13.opExtrude","SWEPT_EDGE",EDGE,{"disambiguationData":[OSD([subQ1,subQ0]),TDD([subQ2])]})]});var subQ12=makeQuery(id+"F15.boolean.opBoolean","MERGE",EDGE,{"derivedFrom":[makeQuery(id+"F14.opExtrude","CAP_EDGE",EDGE,{"disambiguationData":[OSD([subQ1,subQ0]),TDD([subQ11])],"isStart":false}),makeQuery(id+"F15.opExtrude","SWEPT_EDGE",EDGE,{"disambiguationData":[OSD([subQ9,subQ0]),TDD([makeQuery(id+"F14.opExtrude","CAP_VERTEX",VERTEX,{"disambiguationData":[OSD([subQ9,subQ0]),TDD([subQ10])],"isStart":false})])]})]});var subQ13=makeQuery(id+"F19.opExtrude","CAP_EDGE",EDGE,{"disambiguationData":[OSD([subQ1,subQ9,subQ0]),TDD([subQ12])],"isStart":false});var subQ14=makeQuery(id+"F22.opExtrude","CAP_EDGE",EDGE,{"disambiguationData":[OSD([subQ1,subQ9,subQ0]),TDD([subQ13])],"isStart":false});Q0=makeQuery(id+"F40.boolean.opBoolean","MERGE",FACE,{"derivedFrom":[makeQuery(id+"F37.boolean.opBoolean","MERGE",FACE,{"derivedFrom":[makeQuery(id+"F31.boolean.opBoolean","MERGE",FACE,{"derivedFrom":[makeQuery(id+"F25.boolean.opBoolean","MERGE",FACE,{"derivedFrom":[makeQuery(id+"F22.boolean.opBoolean","MERGE",FACE,{"derivedFrom":[makeQuery(id+"F19.boolean.opBoolean","MERGE",FACE,{"derivedFrom":[makeQuery(id+"F15.boolean.opBoolean","MERGE",FACE,{"derivedFrom":[makeQuery(id+"F14.boolean.opBoolean","MERGE",FACE,{"derivedFrom":[makeQuery(id+"F13.boolean.opBoolean","MERGE",FACE,{"derivedFrom":[makeQuery(id+"F12.opExtrude","CAP_FACE",FACE,{"disambiguationData":[OSD([subQ1,subQ9,sQuery(id+"F11.wireOp",EDGE,"E2.left"),subQ0])],"isStart":false}),makeQuery(id+"F13.opExtrude","SWEPT_FACE",FACE,{"disambiguationData":[OSD([subQ1]),TDD([subQ7])]})]}),makeQuery(id+"F14.opExtrude","SWEPT_FACE",FACE,{"disambiguationData":[OSD([subQ1,subQ0]),TDD([subQ11])]})]}),makeQuery(id+"F15.opExtrude","SWEPT_FACE",FACE,{"disambiguationData":[OSD([subQ9,subQ0]),TDD([makeQuery(id+"F14.boolean.opBoolean","MERGE",EDGE,{"derivedFrom":[makeQuery(id+"F12.opExtrude","CAP_EDGE",EDGE,{"disambiguationData":[OSD([subQ9])],"isStart":false}),makeQuery(id+"F14.opExtrude","SWEPT_EDGE",EDGE,{"disambiguationData":[OSD([subQ9,subQ0]),TDD([subQ10])]})]})])]})]}),makeQuery(id+"F19.opExtrude","SWEPT_FACE",FACE,{"disambiguationData":[OSD([subQ1,subQ9,subQ0]),TDD([subQ12])]})]}),makeQuery(id+"F22.opExtrude","SWEPT_FACE",FACE,{"disambiguationData":[OSD([subQ1,subQ9,subQ0]),TDD([subQ13])]})]}),makeQuery(id+"F25.opExtrude","SWEPT_FACE",FACE,{"disambiguationData":[OSD([subQ1,subQ9,subQ0]),TDD([subQ14])]})]}),makeQuery(id+"F31.opExtrude","SWEPT_FACE",FACE,{"disambiguationData":[OSD([subQ1,subQ9,subQ0]),TDD([makeQuery(id+"F25.opExtrude","CAP_EDGE",EDGE,{"disambiguationData":[OSD([subQ1,subQ9,subQ0]),TDD([subQ14])],"isStart":false})])]})]}),makeQuery(id+"F37.opExtrude","SWEPT_FACE",FACE,{"disambiguationData":[OSD([subQ1,subQ0]),TDD([subQ8])]})]}),makeQuery(id+"F40.opExtrude","SWEPT_FACE",FACE,{"disambiguationData":[OSD([subQ1,subQ0]),TDD([makeQuery(id+"F37.opExtrude","CAP_EDGE",EDGE,{"disambiguationData":[OSD([subQ1,subQ0]),TDD([subQ8])],"isStart":false})])]})]});}
            var Q1;
            {var subQ0=sQuery(id+"F0.wireOp",EDGE,"E0.left");var subQ1=sQuery(id+"F0.wireOp",EDGE,"E0.bottom");var subQ2=makeQuery(id+"F1.opExtrude","CAP_VERTEX",VERTEX,{"disambiguationData":[OSD([subQ1,subQ0])],"isStart":false});var subQ3=makeQuery(id+"F2.opExtrude","CAP_VERTEX",VERTEX,{"disambiguationData":[OSD([subQ1,subQ0]),TDD([subQ2])],"isStart":false});var subQ4=makeQuery(id+"F3.opExtrude","CAP_VERTEX",VERTEX,{"disambiguationData":[OSD([subQ1,subQ0]),TDD([subQ3])],"isStart":false});var subQ5=makeQuery(id+"F17.opExtrude","CAP_VERTEX",VERTEX,{"disambiguationData":[OSD([subQ1,subQ0]),TDD([subQ4])],"isStart":false});var subQ6=makeQuery(id+"F20.opExtrude","CAP_VERTEX",VERTEX,{"disambiguationData":[OSD([subQ1,subQ0]),TDD([subQ5])],"isStart":false});var subQ7=makeQuery(id+"F1.opExtrude","CAP_EDGE",EDGE,{"disambiguationData":[OSD([subQ1])],"isStart":false});var subQ8=makeQuery(id+"F29.boolean.opBoolean","MERGE",EDGE,{"derivedFrom":[makeQuery(id+"F23.boolean.opBoolean","MERGE",EDGE,{"derivedFrom":[makeQuery(id+"F20.boolean.opBoolean","MERGE",EDGE,{"derivedFrom":[makeQuery(id+"F17.boolean.opBoolean","MERGE",EDGE,{"derivedFrom":[makeQuery(id+"F3.boolean.opBoolean","MERGE",EDGE,{"derivedFrom":[makeQuery(id+"F2.opExtrude","CAP_EDGE",EDGE,{"disambiguationData":[OSD([subQ1]),TDD([subQ7])],"isStart":false}),makeQuery(id+"F3.opExtrude","SWEPT_EDGE",EDGE,{"disambiguationData":[OSD([subQ1,subQ0]),TDD([subQ3])]})]}),makeQuery(id+"F17.opExtrude","SWEPT_EDGE",EDGE,{"disambiguationData":[OSD([subQ1,subQ0]),TDD([subQ4])]})]}),makeQuery(id+"F20.opExtrude","SWEPT_EDGE",EDGE,{"disambiguationData":[OSD([subQ1,subQ0]),TDD([subQ5])]})]}),makeQuery(id+"F23.opExtrude","SWEPT_EDGE",EDGE,{"disambiguationData":[OSD([subQ1,subQ0]),TDD([subQ6])]})]}),makeQuery(id+"F29.opExtrude","SWEPT_EDGE",EDGE,{"disambiguationData":[OSD([subQ1,subQ0]),TDD([makeQuery(id+"F23.opExtrude","CAP_VERTEX",VERTEX,{"disambiguationData":[OSD([subQ1,subQ0]),TDD([subQ6])],"isStart":false})])]})]});var subQ9=sQuery(id+"F4.wireOp",EDGE,"E1.right");var subQ10=sQuery(id+"F4.wireOp",EDGE,"E1.top");var subQ11=makeQuery(id+"F5.boolean.opBoolean","COPY",VERTEX,{"derivedFrom":makeQuery(id+"F5.opExtrude","CAP_VERTEX",VERTEX,{"disambiguationData":[OSD([subQ10,subQ9])],"isStart":true})});var subQ12=makeQuery(id+"F9.boolean.opBoolean","COPY",VERTEX,{"derivedFrom":makeQuery(id+"F9.opExtrude","CAP_VERTEX",VERTEX,{"disambiguationData":[OSD([subQ10,subQ9]),TDD([subQ11])],"isStart":false})});var subQ13=sQuery(id+"F4.wireOp",EDGE,"E1.bottom");var subQ14=makeQuery(id+"F2.boolean.opBoolean","MERGE",EDGE,{"derivedFrom":[makeQuery(id+"F1.opExtrude","CAP_EDGE",EDGE,{"disambiguationData":[OSD([subQ0])],"isStart":false}),makeQuery(id+"F2.opExtrude","SWEPT_EDGE",EDGE,{"disambiguationData":[OSD([subQ1,subQ0]),TDD([subQ2])]})]});var subQ15=makeQuery(id+"F3.opExtrude","CAP_EDGE",EDGE,{"disambiguationData":[OSD([subQ1,subQ0]),TDD([subQ14])],"isStart":false});var subQ16=makeQuery(id+"F17.opExtrude","CAP_EDGE",EDGE,{"disambiguationData":[OSD([subQ1,subQ0]),TDD([subQ15])],"isStart":false});var subQ17=makeQuery(id+"F20.opExtrude","CAP_EDGE",EDGE,{"disambiguationData":[OSD([subQ1,subQ0]),TDD([subQ16])],"isStart":false});var subQ18=makeQuery(id+"F10.boolean.opBoolean","COPY",VERTEX,{"derivedFrom":makeQuery(id+"F10.opExtrude","CAP_VERTEX",VERTEX,{"disambiguationData":[OSD([subQ10,subQ9]),TDD([subQ12])],"isStart":false})});var subQ19=makeQuery(id+"F18.boolean.opBoolean","COPY",VERTEX,{"derivedFrom":makeQuery(id+"F18.opExtrude","CAP_VERTEX",VERTEX,{"disambiguationData":[OSD([subQ10,subQ9]),TDD([subQ18])],"isStart":false})});var subQ20=sQuery(id+"F4.wireOp",EDGE,"E1.left");Q1=makeQuery(id+"F38.boolean.opBoolean","MERGE",FACE,{"derivedFrom":[makeQuery(id+"F35.boolean.opBoolean","MERGE",FACE,{"derivedFrom":[makeQuery(id+"F33.boolean.opBoolean","MERGE",FACE,{"derivedFrom":[makeQuery(id+"F29.boolean.opBoolean","MERGE",FACE,{"derivedFrom":[makeQuery(id+"F27.boolean.opBoolean","MERGE",FACE,{"derivedFrom":[makeQuery(id+"F23.boolean.opBoolean","MERGE",FACE,{"derivedFrom":[makeQuery(id+"F20.boolean.opBoolean","MERGE",FACE,{"derivedFrom":[makeQuery(id+"F17.boolean.opBoolean","MERGE",FACE,{"derivedFrom":[makeQuery(id+"F3.boolean.opBoolean","MERGE",FACE,{"derivedFrom":[makeQuery(id+"F2.boolean.opBoolean","MERGE",FACE,{"derivedFrom":[makeQuery(id+"F1.opExtrude","CAP_FACE",FACE,{"disambiguationData":[OSD([subQ1,sQuery(id+"F0.wireOp",EDGE,"E0.top"),subQ0,sQuery(id+"F0.wireOp",EDGE,"E0.right")])],"isStart":false}),makeQuery(id+"F2.opExtrude","SWEPT_FACE",FACE,{"disambiguationData":[OSD([subQ1]),TDD([subQ7])]})]}),makeQuery(id+"F3.opExtrude","SWEPT_FACE",FACE,{"disambiguationData":[OSD([subQ1,subQ0]),TDD([subQ14])]})]}),makeQuery(id+"F17.opExtrude","SWEPT_FACE",FACE,{"disambiguationData":[OSD([subQ1,subQ0]),TDD([subQ15])]})]}),makeQuery(id+"F20.opExtrude","SWEPT_FACE",FACE,{"disambiguationData":[OSD([subQ1,subQ0]),TDD([subQ16])]})]}),makeQuery(id+"F23.opExtrude","SWEPT_FACE",FACE,{"disambiguationData":[OSD([subQ1,subQ0]),TDD([subQ17])]})]}),makeQuery(id+"F27.opExtrude","SWEPT_FACE",FACE,{"disambiguationData":[OSD([subQ10,subQ20,subQ9]),TDD([makeQuery(id+"F24.boolean.opBoolean","MERGE",EDGE,{"derivedFrom":[makeQuery(id+"F21.boolean.opBoolean","MERGE",EDGE,{"derivedFrom":[makeQuery(id+"F18.boolean.opBoolean","MERGE",EDGE,{"derivedFrom":[makeQuery(id+"F10.boolean.opBoolean","COPY",EDGE,{"derivedFrom":makeQuery(id+"F10.opExtrude","CAP_EDGE",EDGE,{"disambiguationData":[OSD([subQ10,subQ20,subQ9]),TDD([makeQuery(id+"F9.boolean.opBoolean","MERGE",EDGE,{"derivedFrom":[makeQuery(id+"F6.boolean.opBoolean","MERGE",EDGE,{"derivedFrom":[makeQuery(id+"F5.boolean.opBoolean","COPY",EDGE,{"derivedFrom":makeQuery(id+"F5.opExtrude","CAP_EDGE",EDGE,{"disambiguationData":[OSD([subQ10])],"isStart":true})}),makeQuery(id+"F6.opExtrude","SWEPT_EDGE",EDGE,{"disambiguationData":[OSD([subQ10,subQ20]),TDD([makeQuery(id+"F5.boolean.opBoolean","COPY",VERTEX,{"derivedFrom":makeQuery(id+"F5.opExtrude","CAP_VERTEX",VERTEX,{"disambiguationData":[OSD([subQ10,subQ20])],"isStart":true})})])]})]}),makeQuery(id+"F9.opExtrude","SWEPT_EDGE",EDGE,{"disambiguationData":[OSD([subQ10,subQ9]),TDD([subQ11])]})]})])],"isStart":false})}),makeQuery(id+"F18.opExtrude","SWEPT_EDGE",EDGE,{"disambiguationData":[OSD([subQ10,subQ9]),TDD([subQ18])]})]}),makeQuery(id+"F21.opExtrude","SWEPT_EDGE",EDGE,{"disambiguationData":[OSD([subQ10,subQ9]),TDD([subQ19])]})]}),makeQuery(id+"F24.opExtrude","SWEPT_EDGE",EDGE,{"disambiguationData":[OSD([subQ10,subQ9]),TDD([makeQuery(id+"F21.boolean.opBoolean","COPY",VERTEX,{"derivedFrom":makeQuery(id+"F21.opExtrude","CAP_VERTEX",VERTEX,{"disambiguationData":[OSD([subQ10,subQ9]),TDD([subQ19])],"isStart":false})})])]})]})])]})]}),makeQuery(id+"F29.opExtrude","SWEPT_FACE",FACE,{"disambiguationData":[OSD([subQ1,subQ0]),TDD([makeQuery(id+"F23.opExtrude","CAP_EDGE",EDGE,{"disambiguationData":[OSD([subQ1,subQ0]),TDD([subQ17])],"isStart":false})])]})]}),makeQuery(id+"F33.opExtrude","SWEPT_FACE",FACE,{"disambiguationData":[OSD([subQ13,subQ10,subQ9]),TDD([makeQuery(id+"F30.boolean.opBoolean","COPY",EDGE,{"derivedFrom":makeQuery(id+"F30.opExtrude","CAP_EDGE",EDGE,{"disambiguationData":[OSD([subQ13,subQ10,subQ9]),TDD([makeQuery(id+"F24.boolean.opBoolean","COPY",EDGE,{"derivedFrom":makeQuery(id+"F24.opExtrude","CAP_EDGE",EDGE,{"disambiguationData":[OSD([subQ13,subQ10,subQ9]),TDD([makeQuery(id+"F21.boolean.opBoolean","COPY",EDGE,{"derivedFrom":makeQuery(id+"F21.opExtrude","CAP_EDGE",EDGE,{"disambiguationData":[OSD([subQ13,subQ10,subQ9]),TDD([makeQuery(id+"F18.boolean.opBoolean","COPY",EDGE,{"derivedFrom":makeQuery(id+"F18.opExtrude","CAP_EDGE",EDGE,{"disambiguationData":[OSD([subQ13,subQ10,subQ9]),TDD([makeQuery(id+"F10.boolean.opBoolean","MERGE",EDGE,{"derivedFrom":[makeQuery(id+"F9.boolean.opBoolean","COPY",EDGE,{"derivedFrom":makeQuery(id+"F9.opExtrude","CAP_EDGE",EDGE,{"disambiguationData":[OSD([subQ13,subQ9]),TDD([makeQuery(id+"F8.boolean.opBoolean","MERGE",EDGE,{"derivedFrom":[makeQuery(id+"F5.boolean.opBoolean","COPY",EDGE,{"derivedFrom":makeQuery(id+"F5.opExtrude","CAP_EDGE",EDGE,{"disambiguationData":[OSD([subQ9])],"isStart":true})}),makeQuery(id+"F8.opExtrude","SWEPT_EDGE",EDGE,{"disambiguationData":[OSD([subQ13,subQ9]),TDD([makeQuery(id+"F5.boolean.opBoolean","COPY",VERTEX,{"derivedFrom":makeQuery(id+"F5.opExtrude","CAP_VERTEX",VERTEX,{"disambiguationData":[OSD([subQ13,subQ9])],"isStart":true})})])]})]})])],"isStart":false})}),makeQuery(id+"F10.opExtrude","SWEPT_EDGE",EDGE,{"disambiguationData":[OSD([subQ10,subQ9]),TDD([subQ12])]})]})])],"isStart":false})})])],"isStart":false})})])],"isStart":false})})])],"isStart":false})})])]})]}),makeQuery(id+"F35.opExtrude","SWEPT_FACE",FACE,{"disambiguationData":[OSD([subQ1,subQ0]),TDD([subQ8])]})]}),makeQuery(id+"F38.opExtrude","SWEPT_FACE",FACE,{"disambiguationData":[OSD([subQ1,subQ0]),TDD([makeQuery(id+"F35.opExtrude","CAP_EDGE",EDGE,{"disambiguationData":[OSD([subQ1,subQ0]),TDD([subQ8])],"isStart":false})])]})]});}
            fillet(context, id + "F41", {"entities" : qUnion([Q0, Q1]), "radius" : 3 * mm, "tangentPropagation" : true, "allowEdgeOverflow" : false});
        }
    });
